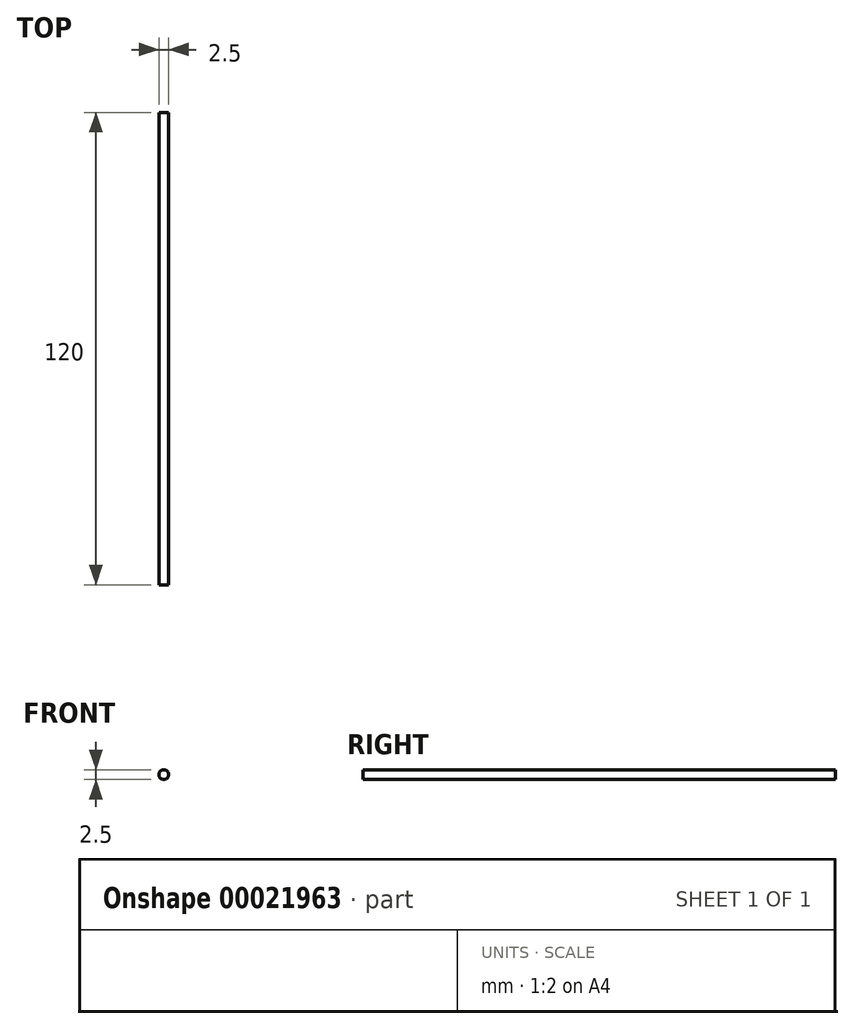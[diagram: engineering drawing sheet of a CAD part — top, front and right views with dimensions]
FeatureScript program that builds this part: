
annotation { "Feature Type Name" : "Feature", "Feature Type Description" : "" }
export const myFeature = defineFeature(function(context is Context, id is Id, definition is map)
    precondition{}
    {
        {
            var Q0;
            Q0=qCreatedBy(makeId("Front.planeOp"),FACE);
            var sketch = newSketch(context, id + "F0", { "sketchPlane" : qUnion([Q0])});
            skCircle(sketch, "E0", {"center": v(-44.87, 13.34) * mm, "radius": 1.25 * mm});
            skSolve(sketch);
        }
        {
            var Q0;
            Q0 = qSketchRegion(id + "F0", true);
            extrude(context, id + "F1", {"entities" : qUnion([Q0]), "endBound" : BoundingType.SYMMETRIC, "depth" : 60 * mm});
        }
        {
            var Q0;
            Q0=makeQuery(id+"F1.opExtrude","CAP_FACE",FACE,{"disambiguationData":[OSD([sQuery(id+"F0.wireOp",EDGE,"E0")])],"isStart":false});
            extrude(context, id + "F2", {"entities" : qUnion([Q0]), "operationType" : NewBodyOperationType.ADD, "depth" : 30 * mm});
        }
        {
            var Q0;
            Q0=makeQuery(id+"F1.opExtrude","CAP_FACE",FACE,{"disambiguationData":[OSD([sQuery(id+"F0.wireOp",EDGE,"E0")])],"isStart":true});
            extrude(context, id + "F3", {"entities" : qUnion([Q0]), "operationType" : NewBodyOperationType.ADD, "depth" : 30 * mm});
        }
    });
